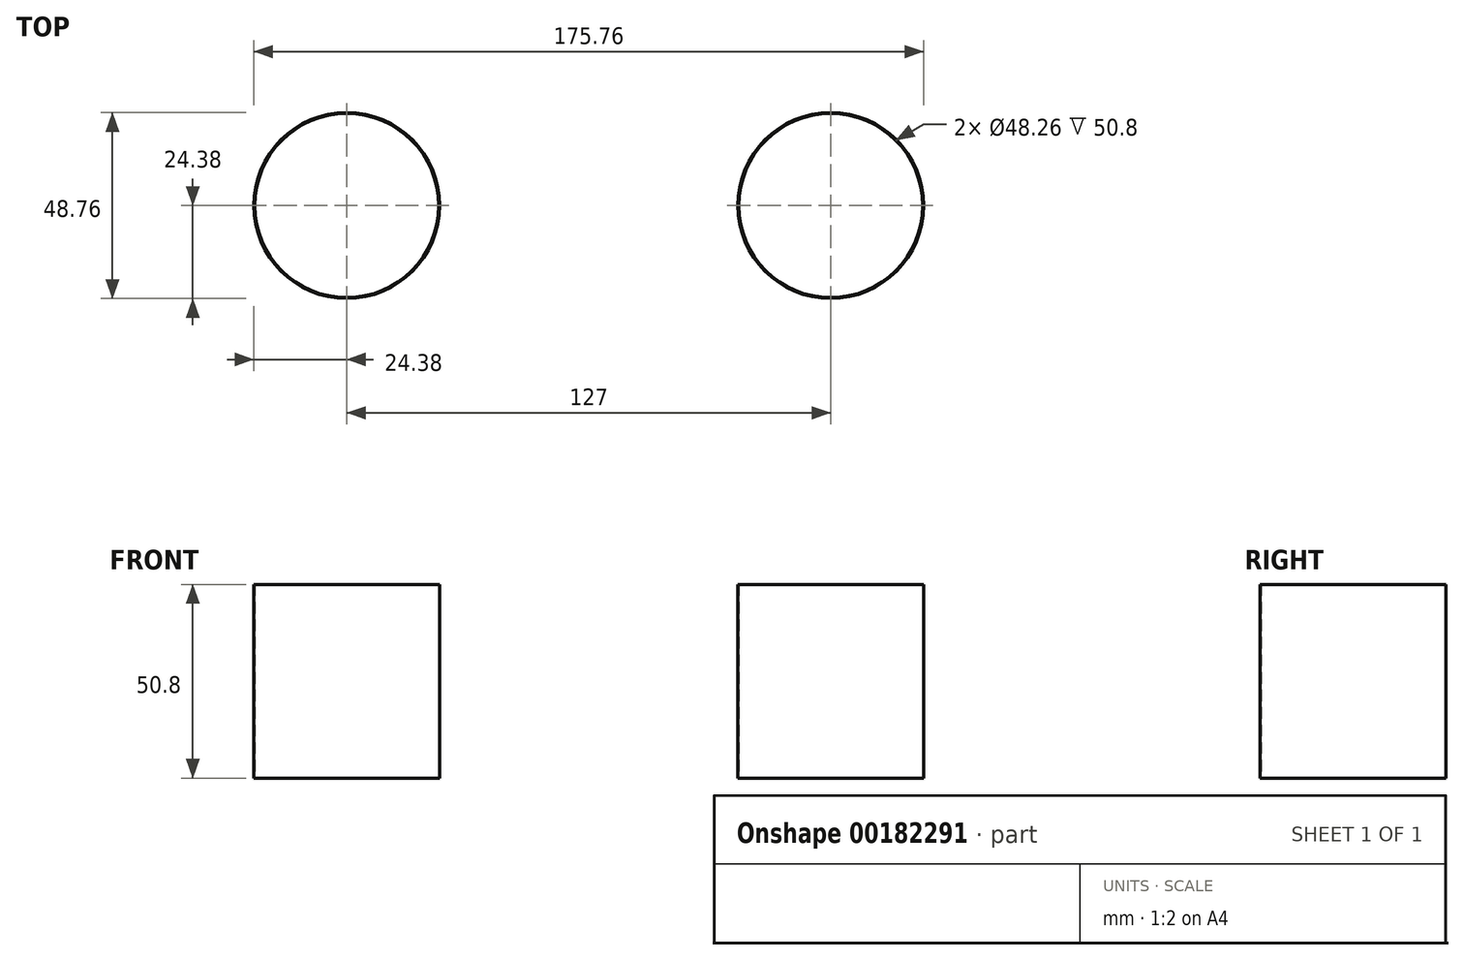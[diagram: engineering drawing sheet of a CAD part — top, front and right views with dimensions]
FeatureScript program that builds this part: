
annotation { "Feature Type Name" : "Feature", "Feature Type Description" : "" }
export const myFeature = defineFeature(function(context is Context, id is Id, definition is map)
    precondition{}
    {
        {
            var Q0;
            Q0=qCreatedBy(makeId("Top.planeOp"),FACE);
            var sketch = newSketch(context, id + "F0", { "sketchPlane" : qUnion([Q0])});
            skCircle(sketch, "E0", {"center": v(0, 0) * mm, "radius": 24.13 * mm});
            skCircle(sketch, "E1.0", {"center": v(0, 0) * mm, "radius": 24.38 * mm});
            skSolve(sketch);
        }
        {
            var Q0;
            Q0 = qSketchRegion(id + "F0", true);
            extrude(context, id + "F1", {"entities" : qUnion([Q0]), "depth" : 50.8 * mm});
        }
        {
            var Q0;
            Q0=makeQuery(id+"F1.opExtrude","SWEPT_BODY",BODY,{"disambiguationData":[OSD([sQuery(id+"F0.wireOp",EDGE,"E0"),sQuery(id+"F0.wireOp",EDGE,"E1.0")])]});
            transform(context, id + "F2", {"entities" : qUnion([Q0]), "transformType" : TransformType.TRANSLATION_3D, "dx" : 127 * mm, "dy" : 0 * mm, "dz" : 0 * mm, "makeCopy" : true});
        }
    });
